# Revit family: CU
name_source: partatom
category: Lighting Devices
revit_build: Autodesk Revit Architecture 2012 (Build: 20110309_2315(x64)
units: mm (PartAtom-declared; Revit-internal decimal feet)

## types (4) — shared parameters
Certifications = Plenum Rated, cULus
Connector Description 1 = Direct Current Power Supply
Connector Description 2 = Alternating Current Power Supply
Connector Description 3 = Controls
DC Voltage = 24 V
Description = Automatic-ON operation, 120/277V AC, 50/60Hz for use with 1 to 4 ATD, ATU and ATP series 
ceiling/wall mount sensors
Electrical Ratings = 120V AC: 800W Incandescent, 1000W Fluorescent, 1/6 HP; 277V AC: 1800W Fluorescent, 1/6 HP
Frequency = 60 Hz
Humidity = 0% to 90% non condensing 
relative humidity
Load Classification = Power
Manufacturer = Hubbell Wiring Device-Kellems
Number of Poles = 1
Power Factor = 1
Power Factor 2 = 1
Product Documentation Link = http://ecatalog.hubbell-wiring.com
Product Material = Plastic - Hubbell - Black
Product Page URL = http://www.hubbell-wiring.com
URL = http://www.hubbell-wiring.com
zero-valued in all types: Default Elevation

## per-type parameters (varying)
| type | AC Voltage | Apparent Load | Apparent Load 2 | Automatic ON | Horse Power | Manual ON | Operating Temperature | Type Selector | UPC Number |
| CU300A | 120 V | 3.600 VA | 1800.000 VA | No | 0 | Yes | 32°F to 104°F (0°C to 40°C) | CU300A-M : CU300A | 783585181004 |
| CU300M | 120 V | 3.600 VA | 1800.000 VA | No | 0 | Yes | 32°F to 104°F (0°C to 40°C) | CU300A-M : CU300M | 783585159362 |
| CU347A | 347 V | 2.400 VA | 5205.000 VA | Yes | 0 | No | 32°F to 104°F (0°C to 40°C) | CU347A | 783585349350 |
| CU300HD | 277 V | 6.000 VA | 5540.000 VA | Yes | 2 | Yes | -40°F to 149°F (-40°C to 65°C) | CU300HD | 783585256207 |

note: column(s) folded — value = type name in every type: Model

## geometry (parser evidence)
native form markers: Blend x1, Sweep x8
no freeform markers — native parametric forms only
